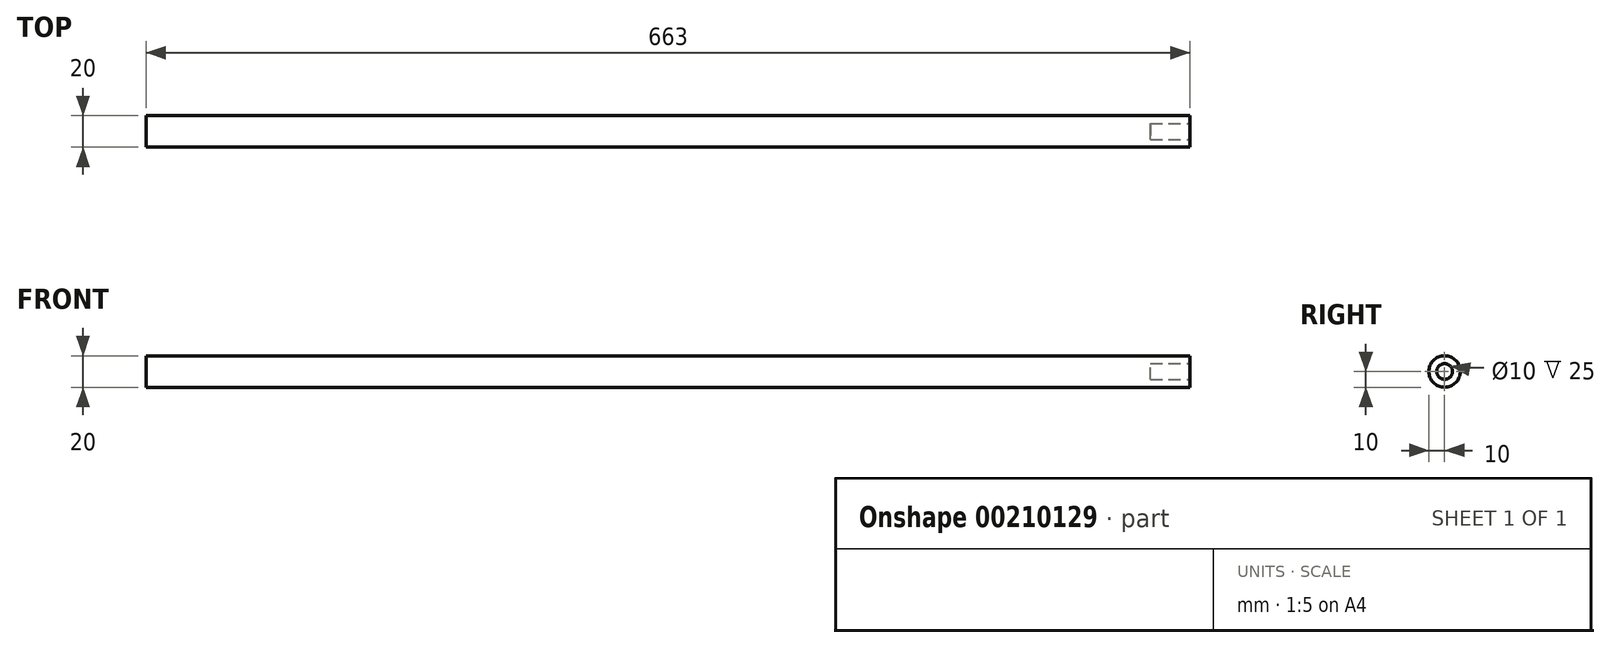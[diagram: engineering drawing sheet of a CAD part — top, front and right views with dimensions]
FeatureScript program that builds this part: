
annotation { "Feature Type Name" : "Feature", "Feature Type Description" : "" }
export const myFeature = defineFeature(function(context is Context, id is Id, definition is map)
    precondition{}
    {
        {
            var Q0;
            Q0=qCreatedBy(makeId("Right.planeOp"),FACE);
            var sketch = newSketch(context, id + "F0", { "sketchPlane" : qUnion([Q0])});
            skCircle(sketch, "E0", {"center": v(0, 0) * mm, "radius": 10 * mm});
            skSolve(sketch);
        }
        {
            var Q0;
            Q0 = qSketchRegion(id + "F0", true);
            extrude(context, id + "F1", {"entities" : qUnion([Q0]), "depth" : 638 * mm});
        }
        {
            var Q0;
            Q0=makeQuery(id+"F1.opExtrude","CAP_FACE",FACE,{"disambiguationData":[OSD([sQuery(id+"F0.wireOp",EDGE,"E0")])],"isStart":false});
            extrude(context, id + "F2", {"entities" : qUnion([Q0]), "operationType" : NewBodyOperationType.ADD, "depth" : 25 * mm});
        }
        {
            var Q0;
            Q0=makeQuery(id+"F2.opExtrude","CAP_FACE",FACE,{"disambiguationData":[OSD([sQuery(id+"F0.wireOp",EDGE,"E0")])],"isStart":false});
            var sketch = newSketch(context, id + "F3", { "sketchPlane" : qUnion([Q0])});
            skCircle(sketch, "E1", {"center": v(0, 0) * mm, "radius": 5 * mm});
            skSolve(sketch);
        }
        {
            var Q0;
            Q0 = qSketchRegion(id + "F3", true);
            extrude(context, id + "F4", {"entities" : qUnion([Q0]), "operationType" : NewBodyOperationType.REMOVE, "oppositeDirection" : true, "depth" : 25 * mm});
        }
    });
